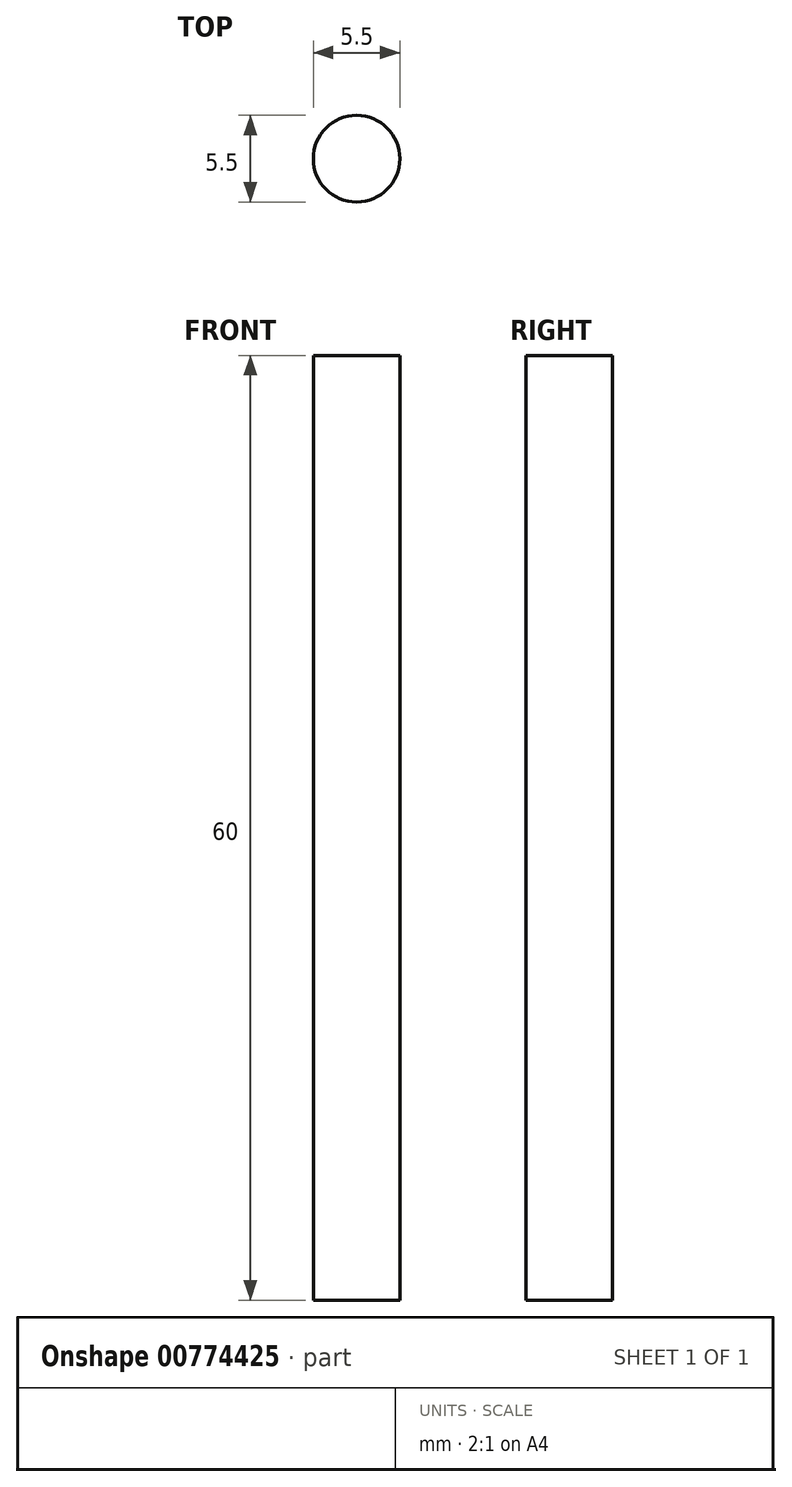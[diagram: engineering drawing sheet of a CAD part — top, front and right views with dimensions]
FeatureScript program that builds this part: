
annotation { "Feature Type Name" : "Feature", "Feature Type Description" : "" }
export const myFeature = defineFeature(function(context is Context, id is Id, definition is map)
    precondition{}
    {
        {
            var Q0;
            Q0=qCreatedBy(makeId("Top.planeOp"),FACE);
            var sketch = newSketch(context, id + "F0", { "sketchPlane" : qUnion([Q0])});
            skCircle(sketch, "E0", {"center": v(0, 0) * mm, "radius": 2.75 * mm});
            skSolve(sketch);
        }
        {
            var Q0;
            Q0 = qSketchRegion(id + "F0", true);
            extrude(context, id + "F1", {"entities" : qUnion([Q0]), "depth" : 60 * mm, "offsetDistance" : 25 * mm});
        }
    });
